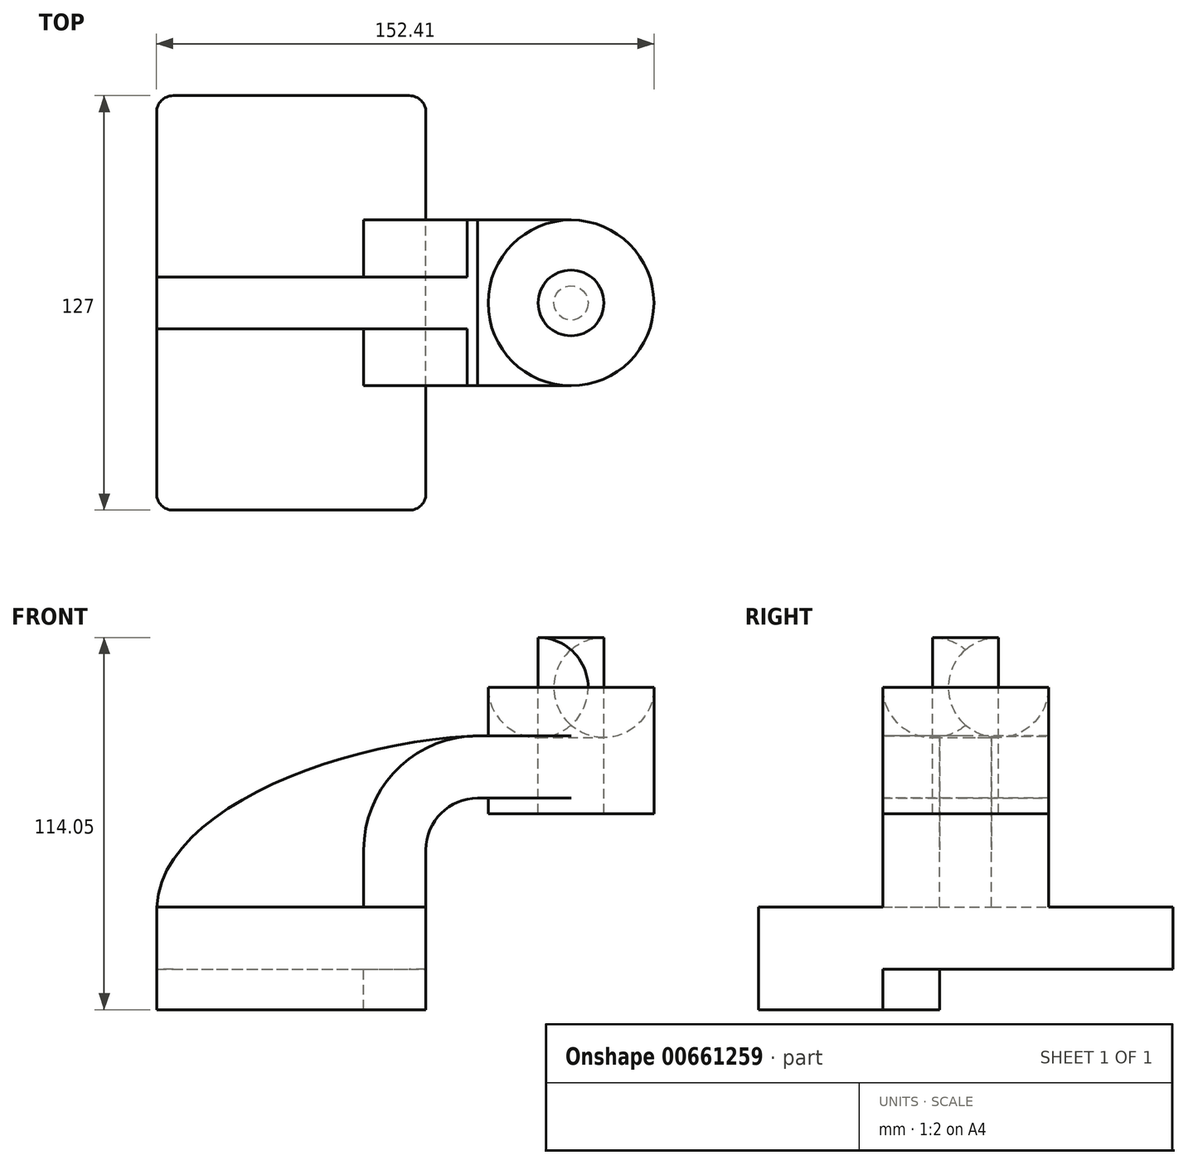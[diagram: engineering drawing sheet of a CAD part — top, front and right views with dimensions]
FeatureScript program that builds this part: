
annotation { "Feature Type Name" : "Feature", "Feature Type Description" : "" }
export const myFeature = defineFeature(function(context is Context, id is Id, definition is map)
    precondition{}
    {
        {
            var Q0;
            Q0=qCreatedBy(makeId("Front.planeOp"),FACE);
            var sketch = newSketch(context, id + "F0", { "sketchPlane" : qUnion([Q0])});
            skLineSegment(sketch, "E0.rect.bottom", {"start": v(-41.28, 9.52) * mm, "end": v(41.28, 9.52) * mm});
            skLineSegment(sketch, "E0.rect.top", {"start": v(-41.28, -9.52) * mm, "end": v(41.28, -9.52) * mm});
            skLineSegment(sketch, "E0.rect.left", {"start": v(-41.28, 9.52) * mm, "end": v(-41.28, -9.52) * mm});
            skLineSegment(sketch, "E0.rect.right", {"start": v(41.28, 9.52) * mm, "end": v(41.28, -9.52) * mm});
            skPoint(sketch, "E0.rect.middle", {"position": v(0, 0) * mm});
            skLineSegment(sketch, "E1", {"start": v(41.28, 9.52) * mm, "end": v(41.28, 27) * mm});
            skArc(sketch, "E2", {"start": v(41.28, 27) * mm, "mid": v(45.92, 38.23) * mm, "end": v(57.15, 42.88) * mm});
            skLineSegment(sketch, "E3", {"start": v(57.15, 42.88) * mm, "end": v(85.72, 42.88) * mm});
            skLineSegment(sketch, "E4.rect.bottom", {"start": v(60.32, 38.1) * mm, "end": v(111.12, 38.1) * mm});
            skLineSegment(sketch, "E4.rect.top", {"start": v(60.32, 66.68) * mm, "end": v(111.12, 66.68) * mm});
            skLineSegment(sketch, "E4.rect.left", {"start": v(60.32, 38.1) * mm, "end": v(60.32, 66.68) * mm});
            skLineSegment(sketch, "E4.rect.right", {"start": v(111.13, 38.1) * mm, "end": v(111.12, 66.68) * mm});
            skPoint(sketch, "E4.rect.middle", {"position": v(85.72, 52.39) * mm});
            skLineSegment(sketch, "E5.0", {"start": v(57.15, 61.93) * mm, "end": v(85.72, 61.93) * mm});
            skArc(sketch, "E5.1", {"start": v(22.23, 27) * mm, "mid": v(32.45, 51.7) * mm, "end": v(57.15, 61.93) * mm});
            skLineSegment(sketch, "E5.2", {"start": v(22.23, 9.52) * mm, "end": v(22.23, 27) * mm});
            skLineSegment(sketch, "E6", {"start": v(85.72, 38.1) * mm, "end": v(85.72, 66.68) * mm});
            skFitSpline(sketch, "E7", {"points": [v(-41.28, 9.53) * mm, v(57.15, 61.93) * mm], "startDerivative": vector(5.2, 92.34) * mm, "endDerivative": vector(120.92, 4.22) * mm});
            skSolve(sketch);
        }
        {
            var Q0;
            Q0=makeQuery(id+"F0.imprint","IMPRINT",FACE,{"disambiguationData":[TD([[makeQuery(id+"F0.imprint","IMPRINT",EDGE,{"derivedFrom":sQuery(id+"F0.wireOp",EDGE,"E0.rect.top")}),1.0]])]});
            extrude(context, id + "F1", {"entities" : qUnion([Q0]), "endBound" : BoundingType.SYMMETRIC, "depth" : 127 * mm});
        }
        {
            var Q0;
            {var subQ9=sQuery(id+"F0.wireOp",EDGE,"E1");Q0=makeQuery(id+"F0.imprint","IMPRINT",FACE,{"disambiguationData":[TD([[makeQuery(id+"F0.imprint","IMPRINT",EDGE,{"derivedFrom":subQ9}),1.0]])]});}
            var Q1;
            {var subQ0=sQuery(id+"F0.wireOp",EDGE,"E6");var subQ1=sQuery(id+"F0.wireOp",EDGE,"E3");var subQ2=makeQuery(id+"F0.imprint","INTERSECT",VERTEX,{"derivedFrom":[subQ1,subQ0]});Q1=makeQuery(id+"F0.imprint","IMPRINT",FACE,{"disambiguationData":[TD([[makeQuery(id+"F0.imprint","IMPRINT",EDGE,{"disambiguationData":[TD([[subQ2,1.0]])],"derivedFrom":subQ1}),1.0]])]});}
            extrude(context, id + "F2", {"entities" : qUnion([Q0, Q1]), "operationType" : NewBodyOperationType.ADD, "endBound" : BoundingType.SYMMETRIC, "depth" : 50.8 * mm});
        }
        {
            var Q0;
            {var subQ3=sQuery(id+"F0.wireOp",EDGE,"E5.2");Q0=makeQuery(id+"F0.imprint","IMPRINT",FACE,{"disambiguationData":[TD([[makeQuery(id+"F0.imprint","IMPRINT",EDGE,{"derivedFrom":subQ3}),1.0]])]});}
            extrude(context, id + "F3", {"entities" : qUnion([Q0]), "operationType" : NewBodyOperationType.ADD, "endBound" : BoundingType.SYMMETRIC, "depth" : 15.88 * mm});
        }
        {
            var Q0;
            {var subQ5=sQuery(id+"F0.wireOp",EDGE,"E4.rect.right");Q0=makeQuery(id+"F0.imprint","IMPRINT",FACE,{"disambiguationData":[TD([[makeQuery(id+"F0.imprint","IMPRINT",EDGE,{"derivedFrom":subQ5}),1.0]])]});}
            var Q1;
            Q1=sQuery(id+"F0.wireOp",EDGE,"E6");
            revolve(context, id + "F4", {"operationType" : NewBodyOperationType.ADD, "entities" : qUnion([Q0]), "axis" : qUnion([Q1]), "revolveType" : RevolveType.FULL});
        }
        {
            var Q0;
            Q0=makeQuery(id+"F1.opExtrude","CAP_EDGE",EDGE,{"disambiguationData":[OSD([sQuery(id+"F0.wireOp",EDGE,"E0.rect.right")])],"isStart":false});
            var Q1;
            Q1=makeQuery(id+"F1.opExtrude","CAP_EDGE",EDGE,{"disambiguationData":[OSD([sQuery(id+"F0.wireOp",EDGE,"E0.rect.left")])],"isStart":false});
            var Q2;
            Q2=makeQuery(id+"F1.opExtrude","CAP_EDGE",EDGE,{"disambiguationData":[OSD([sQuery(id+"F0.wireOp",EDGE,"E0.rect.right")])],"isStart":true});
            var Q3;
            Q3=makeQuery(id+"F1.opExtrude","CAP_EDGE",EDGE,{"disambiguationData":[OSD([sQuery(id+"F0.wireOp",EDGE,"E0.rect.left")])],"isStart":true});
            fillet(context, id + "F5", {"entities" : qUnion([Q0, Q1, Q2, Q3]), "radius" : 5.08 * mm, "tangentPropagation" : true, "allowEdgeOverflow" : false});
        }
        {
            var Q0;
            {var subQ4=sQuery(id+"F0.wireOp",EDGE,"E0.rect.bottom");var subQ5=sQuery(id+"F0.wireOp",EDGE,"E0.rect.right");var subQ6=sQuery(id+"F0.wireOp",EDGE,"E0.rect.left");Q0=makeQuery(id+"F3.boolean.opBoolean","SPLIT",FACE,{"disambiguationData":[TD([makeQuery(id+"F1.opExtrude","CAP_FACE",FACE,{"disambiguationData":[OSD([subQ4,sQuery(id+"F0.wireOp",EDGE,"E0.rect.top"),subQ6,subQ5])],"isStart":false})])],"derivedFrom":makeQuery(id+"F1.opExtrude","SWEPT_FACE",FACE,{"disambiguationData":[OSD([subQ4])]})});}
            var sketch = newSketch(context, id + "F6", { "sketchPlane" : qUnion([Q0])});
            skLineSegment(sketch, "E8.bottom", {"start": v(-13.12, -41.31) * mm, "end": v(13.19, -41.31) * mm});
            skLineSegment(sketch, "E8.top", {"start": v(-13.12, -25.55) * mm, "end": v(13.19, -25.55) * mm});
            skLineSegment(sketch, "E8.left", {"start": v(-13.12, -41.31) * mm, "end": v(-13.12, -25.55) * mm});
            skLineSegment(sketch, "E8.right", {"start": v(13.19, -41.31) * mm, "end": v(13.19, -25.55) * mm});
            skSolve(sketch);
        }
        {
            var Q0;
            Q0 = qSketchRegion(id + "F6", true);
            var Q1;
            Q1=makeQuery(id+"F6.imprint","IMPRINT",FACE,{"disambiguationData":[TD([[makeQuery(id+"F6.imprint","IMPRINT",EDGE,{"derivedFrom":sQuery(id+"F6.wireOp",EDGE,"E8.bottom")}),-1.0]])]});
            extrude(context, id + "F7", {"entities" : qUnion([Q0, Q1]), "operationType" : NewBodyOperationType.ADD, "oppositeDirection" : true, "depth" : 31.5 * mm, "offsetDistance" : 25.4 * mm});
        }
        {
            var Q0;
            {var subQ0=sQuery(id+"F0.wireOp",EDGE,"E0.rect.bottom");Q0=makeQuery(id+"F7.boolean.opBoolean","MERGE",FACE,{"derivedFrom":[makeQuery(id+"F1.opExtrude","CAP_FACE",FACE,{"disambiguationData":[OSD([subQ0,sQuery(id+"F0.wireOp",EDGE,"E0.rect.top"),sQuery(id+"F0.wireOp",EDGE,"E0.rect.left"),sQuery(id+"F0.wireOp",EDGE,"E0.rect.right")])],"isStart":false}),makeQuery(id+"F7.opExtrude","SWEPT_FACE",FACE,{"disambiguationData":[OSD([subQ0]),TDD([makeQuery(id+"F6.imprint","IMPRINT",EDGE,{"derivedFrom":makeQuery(id+"F1.opExtrude","CAP_EDGE",EDGE,{"disambiguationData":[OSD([subQ0])],"isStart":false})})])]})]});}
            extrude(context, id + "F8", {"entities" : qUnion([Q0]), "operationType" : NewBodyOperationType.ADD, "oppositeDirection" : true, "depth" : 33.27 * mm, "offsetDistance" : 25.4 * mm});
        }
        {
            var Q0;
            Q0=makeQuery(id+"F4.opRevolve","SWEPT_FACE",FACE,{"disambiguationData":[OSD([sQuery(id+"F0.wireOp",EDGE,"E4.rect.top")])]});
            extrude(context, id + "F9", {"entities" : qUnion([Q0]), "operationType" : NewBodyOperationType.ADD, "depth" : 25.4 * mm, "offsetDistance" : 25.4 * mm});
        }
        {
            var Q0;
            Q0=makeQuery(id+"F9.opExtrude","CAP_EDGE",EDGE,{"disambiguationData":[OSD([sQuery(id+"F0.wireOp",EDGE,"E4.rect.top"),sQuery(id+"F0.wireOp",EDGE,"E4.rect.right")])],"isStart":false});
            fillet(context, id + "F10", {"entities" : qUnion([Q0]), "radius" : 15.33 * mm, "tangentPropagation" : true, "allowEdgeOverflow" : false});
        }
        {
            var Q0;
            Q0=makeQuery(id+"F2.opExtrude","CAP_FACE",FACE,{"disambiguationData":[OSD([sQuery(id+"F0.wireOp",EDGE,"E0.rect.bottom"),sQuery(id+"F0.wireOp",EDGE,"E1"),sQuery(id+"F0.wireOp",EDGE,"E2"),sQuery(id+"F0.wireOp",EDGE,"E3"),sQuery(id+"F0.wireOp",EDGE,"E5.0"),sQuery(id+"F0.wireOp",EDGE,"E5.1"),sQuery(id+"F0.wireOp",EDGE,"E5.2"),sQuery(id+"F0.wireOp",EDGE,"E6"),sQuery(id+"F0.wireOp",EDGE,"E7")])],"isStart":false});
            extrude(context, id + "F11", {"entities" : qUnion([Q0]), "operationType" : NewBodyOperationType.ADD, "oppositeDirection" : true, "depth" : 11.43 * mm, "offsetDistance" : 25.4 * mm});
        }
        {
            var Q0;
            Q0=makeQuery(id+"F9.opExtrude","CAP_FACE",FACE,{"disambiguationData":[OSD([sQuery(id+"F0.wireOp",EDGE,"E4.rect.top")])],"isStart":false});
            extrude(context, id + "F12", {"entities" : qUnion([Q0]), "operationType" : NewBodyOperationType.REMOVE, "oppositeDirection" : true, "depth" : 106.17 * mm, "offsetDistance" : 25.4 * mm});
        }
    });
